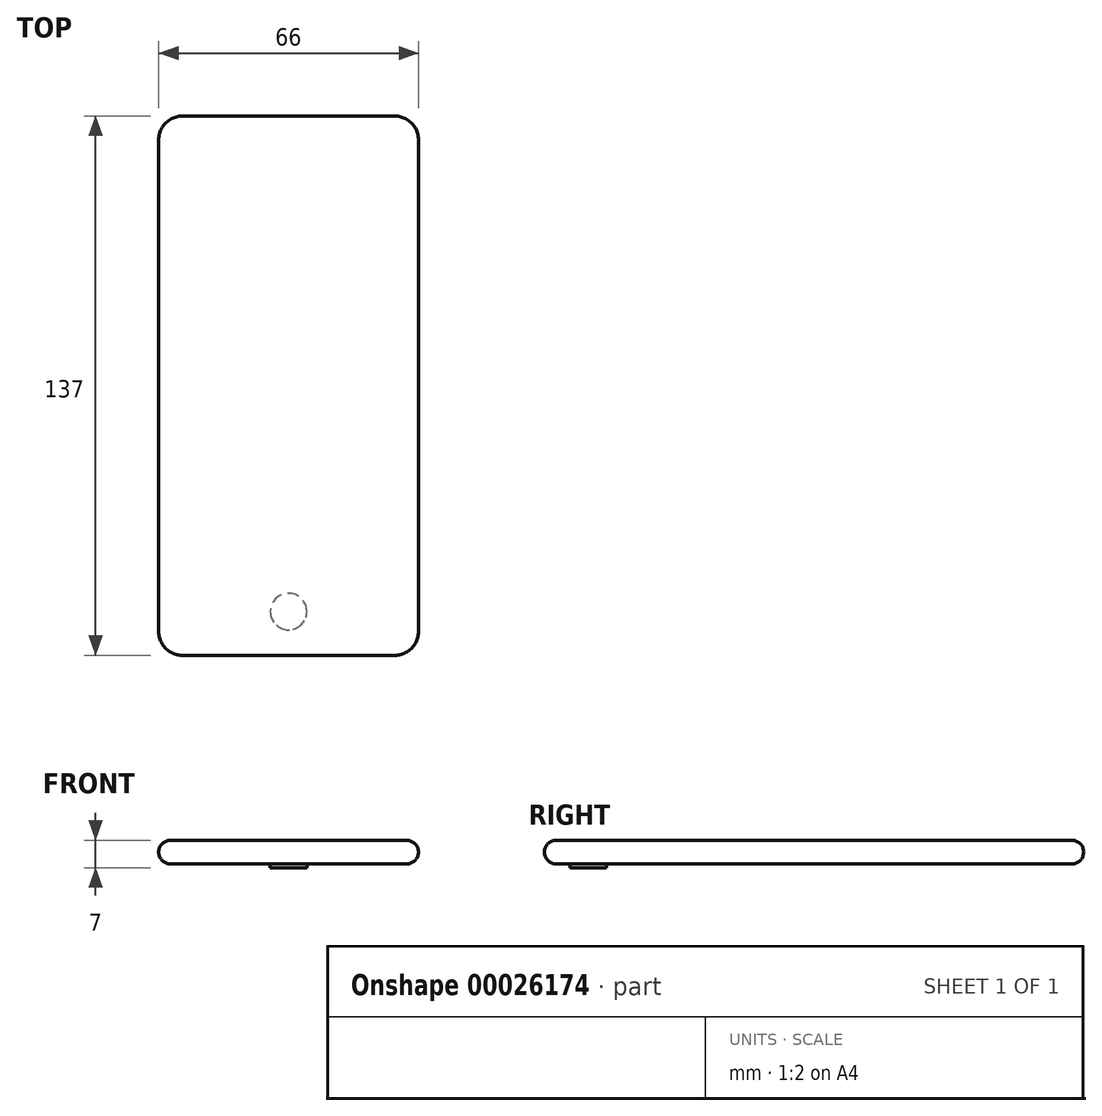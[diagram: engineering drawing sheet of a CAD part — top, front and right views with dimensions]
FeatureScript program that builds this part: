
annotation { "Feature Type Name" : "Feature", "Feature Type Description" : "" }
export const myFeature = defineFeature(function(context is Context, id is Id, definition is map)
    precondition{}
    {
        {
            var Q0;
            Q0=qCreatedBy(makeId("Top.planeOp"),FACE);
            var sketch = newSketch(context, id + "F0", { "sketchPlane" : qUnion([Q0])});
            skLineSegment(sketch, "E0.rect.bottom", {"start": v(-33, 68.5) * mm, "end": v(33, 68.5) * mm});
            skLineSegment(sketch, "E0.rect.top", {"start": v(-33, -68.5) * mm, "end": v(33, -68.5) * mm});
            skLineSegment(sketch, "E0.rect.left", {"start": v(-33, 68.5) * mm, "end": v(-33, -68.5) * mm});
            skLineSegment(sketch, "E0.rect.right", {"start": v(33, 68.5) * mm, "end": v(33, -68.5) * mm});
            skPoint(sketch, "E0.rect.middle", {"position": v(0, 0) * mm});
            skSolve(sketch);
        }
        {
            var Q0;
            Q0=makeQuery(id+"F0.imprint","IMPRINT",FACE,{"disambiguationData":[TD([[makeQuery(id+"F0.imprint","IMPRINT",EDGE,{"derivedFrom":sQuery(id+"F0.wireOp",EDGE,"E0.rect.bottom")}),-1.0]])]});
            extrude(context, id + "F1", {"entities" : qUnion([Q0]), "depth" : 6 * mm});
        }
        {
            var Q0;
            Q0=makeQuery(id+"F1.opExtrude","SWEPT_EDGE",EDGE,{"disambiguationData":[OSD([sQuery(id+"F0.wireOp",EDGE,"E0.rect.top"),sQuery(id+"F0.wireOp",EDGE,"E0.rect.right")])]});
            var Q1;
            Q1=makeQuery(id+"F1.opExtrude","SWEPT_EDGE",EDGE,{"disambiguationData":[OSD([sQuery(id+"F0.wireOp",EDGE,"E0.rect.bottom"),sQuery(id+"F0.wireOp",EDGE,"E0.rect.right")])]});
            var Q2;
            Q2=makeQuery(id+"F1.opExtrude","SWEPT_EDGE",EDGE,{"disambiguationData":[OSD([sQuery(id+"F0.wireOp",EDGE,"E0.rect.bottom"),sQuery(id+"F0.wireOp",EDGE,"E0.rect.left")])]});
            var Q3;
            Q3=makeQuery(id+"F1.opExtrude","SWEPT_EDGE",EDGE,{"disambiguationData":[OSD([sQuery(id+"F0.wireOp",EDGE,"E0.rect.top"),sQuery(id+"F0.wireOp",EDGE,"E0.rect.left")])]});
            fillet(context, id + "F2", {"entities" : qUnion([Q0, Q1, Q2, Q3]), "radius" : 6 * mm, "tangentPropagation" : true, "allowEdgeOverflow" : false});
        }
        {
            var Q0;
            Q0=makeQuery(id+"F1.opExtrude","CAP_FACE",FACE,{"disambiguationData":[OSD([sQuery(id+"F0.wireOp",EDGE,"E0.rect.bottom"),sQuery(id+"F0.wireOp",EDGE,"E0.rect.top"),sQuery(id+"F0.wireOp",EDGE,"E0.rect.left"),sQuery(id+"F0.wireOp",EDGE,"E0.rect.right")])],"isStart":false});
            var Q1;
            Q1=makeQuery(id+"F1.opExtrude","CAP_FACE",FACE,{"disambiguationData":[OSD([sQuery(id+"F0.wireOp",EDGE,"E0.rect.bottom"),sQuery(id+"F0.wireOp",EDGE,"E0.rect.top"),sQuery(id+"F0.wireOp",EDGE,"E0.rect.left"),sQuery(id+"F0.wireOp",EDGE,"E0.rect.right")])],"isStart":true});
            fillet(context, id + "F3", {"entities" : qUnion([Q0, Q1]), "radius" : 3 * mm, "tangentPropagation" : true, "allowEdgeOverflow" : false});
        }
        {
            var Q0;
            Q0=makeQuery(id+"F1.opExtrude","CAP_FACE",FACE,{"disambiguationData":[OSD([sQuery(id+"F0.wireOp",EDGE,"E0.rect.bottom"),sQuery(id+"F0.wireOp",EDGE,"E0.rect.top"),sQuery(id+"F0.wireOp",EDGE,"E0.rect.left"),sQuery(id+"F0.wireOp",EDGE,"E0.rect.right")])],"isStart":true});
            var sketch = newSketch(context, id + "F4", { "sketchPlane" : qUnion([Q0])});
            skCircle(sketch, "E1", {"center": v(0, 57.4) * mm, "radius": 4.65 * mm});
            skSolve(sketch);
        }
        {
            var Q0;
            Q0=makeQuery(id+"F4.imprint","IMPRINT",FACE,{"disambiguationData":[TD([[makeQuery(id+"F4.imprint","IMPRINT",EDGE,{"derivedFrom":sQuery(id+"F4.wireOp",EDGE,"E1")}),1.0]])]});
            extrude(context, id + "F5", {"entities" : qUnion([Q0]), "operationType" : NewBodyOperationType.ADD, "depth" : 1 * mm});
        }
    });
